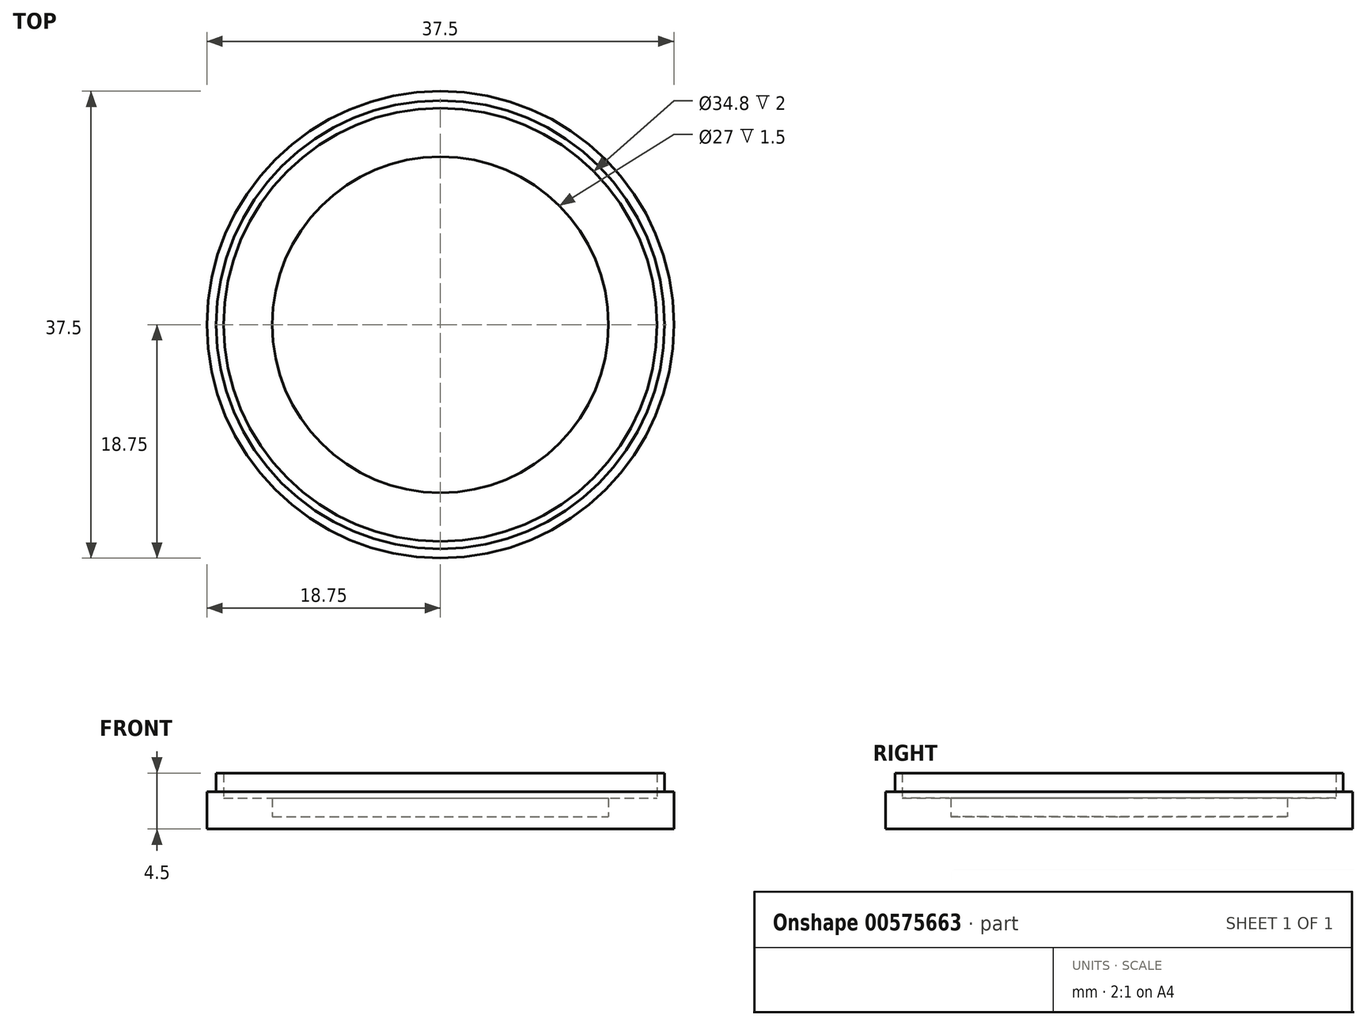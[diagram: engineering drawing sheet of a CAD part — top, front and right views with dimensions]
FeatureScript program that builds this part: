
annotation { "Feature Type Name" : "Feature", "Feature Type Description" : "" }
export const myFeature = defineFeature(function(context is Context, id is Id, definition is map)
    precondition{}
    {
        {
            var Q0;
            Q0=qCreatedBy(makeId("Front.planeOp"),FACE);
            var sketch = newSketch(context, id + "F0", { "sketchPlane" : qUnion([Q0])});
            skLineSegment(sketch, "E0", {"start": v(0, 0) * mm, "end": v(18.75, 0) * mm});
            skLineSegment(sketch, "E1", {"start": v(18.75, 0) * mm, "end": v(18.75, 3) * mm});
            skLineSegment(sketch, "E2", {"start": v(18.75, 3) * mm, "end": v(18, 3) * mm});
            skLineSegment(sketch, "E3", {"start": v(18, 3) * mm, "end": v(18, 4.5) * mm});
            skLineSegment(sketch, "E4", {"start": v(18, 4.5) * mm, "end": v(17.4, 4.5) * mm});
            skLineSegment(sketch, "E5", {"start": v(13.5, 1) * mm, "end": v(0, 1) * mm});
            skLineSegment(sketch, "E6", {"start": v(0, 0) * mm, "end": v(0, 26.67) * mm, "construction": true});
            skLineSegment(sketch, "E7", {"start": v(17.4, 4.5) * mm, "end": v(17.4, 2.5) * mm});
            skLineSegment(sketch, "E8", {"start": v(17.4, 2.5) * mm, "end": v(13.5, 2.5) * mm});
            skLineSegment(sketch, "E9", {"start": v(13.5, 2.5) * mm, "end": v(13.5, 1) * mm});
            skLineSegment(sketch, "E10", {"start": v(0, 1) * mm, "end": v(0, 0) * mm});
            skSolve(sketch);
        }
        {
            var Q0;
            Q0 = qSketchRegion(id + "F0", true);
            var Q1;
            Q1=sQuery(id+"F0.wireOp",EDGE,"E6");
            revolve(context, id + "F1", {"entities" : qUnion([Q0]), "axis" : qUnion([Q1]), "revolveType" : RevolveType.FULL});
        }
    });
